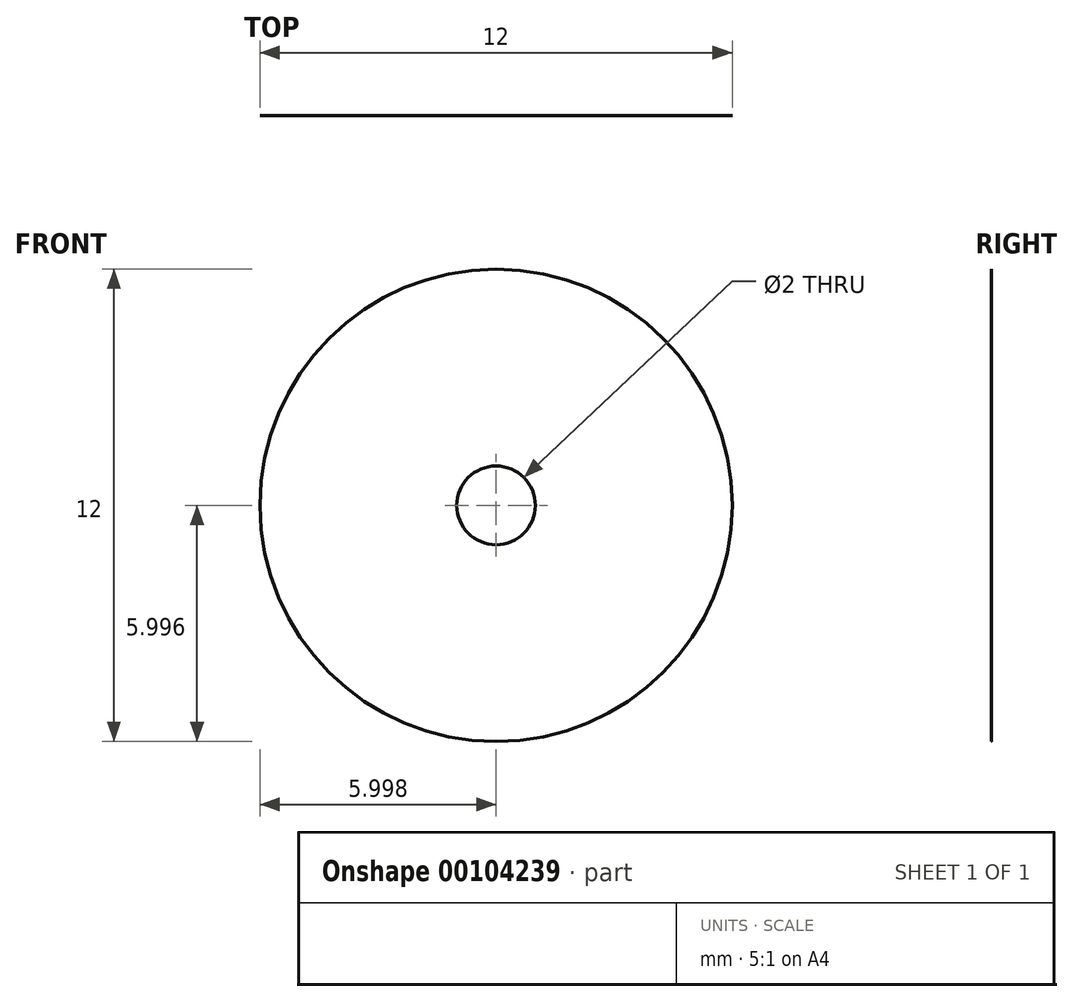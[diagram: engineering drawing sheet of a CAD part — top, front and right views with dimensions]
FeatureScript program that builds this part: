
annotation { "Feature Type Name" : "Feature", "Feature Type Description" : "" }
export const myFeature = defineFeature(function(context is Context, id is Id, definition is map)
    precondition{}
    {
        {
            var Q0;
            Q0=qCreatedBy(makeId("Front.planeOp"),FACE);
            var sketch = newSketch(context, id + "F0", { "sketchPlane" : qUnion([Q0])});
            skCircle(sketch, "E0", {"center": v(-37.81, 24.96) * mm, "radius": 6 * mm});
            skCircle(sketch, "E1", {"center": v(-37.81, 24.96) * mm, "radius": 1 * mm});
            skSolve(sketch);
        }
        {
            var Q0;
            Q0=makeQuery(id+"F0.imprint","IMPRINT",FACE,{"disambiguationData":[TD([[makeQuery(id+"F0.imprint","IMPRINT",EDGE,{"derivedFrom":sQuery(id+"F0.wireOp",EDGE,"E0")}),1.0]])]});
            extrude(context, id + "F1", {"entities" : qUnion([Q0]), "depth" : 1 / 203.2 * mm});
        }
    });
